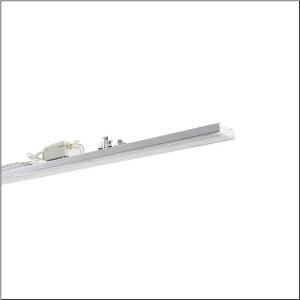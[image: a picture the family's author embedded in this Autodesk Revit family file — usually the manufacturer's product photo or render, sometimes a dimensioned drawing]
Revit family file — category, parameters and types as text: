
# Revit family: licross_11_recessed_extreme_mo_51te18dv4e5ge
name_source: partatom
category: Lighting Fixtures
units: mm (PartAtom-declared; Revit-internal decimal feet)

## family parameters
Cut with Voids When Loaded = No
Host = Face
Light Source = No
Part Type = Normal
Room Calculation Point = No
Round Connector Dimension = Use Diameter
Shared = No

## types (1)
- --- (1 x LED, 14980 lm, 84.5 W, 4000K)
    Apparent Load = 85 VA
    CIE Flux Codes = 83 96 99 100 100
    Color Rendering = 80
    Color Temperature = 4000K
    Default Elevation = 1800 mm
    Description = Licross 11 Recessed extreme MO, luminaire insert, of sheet steel, galvanised, coil coated, white, length: 2.250mm, width: 66mm, height: 67mm, LED rated luminous flux: 14.980lm, light colour: 840, SDCM (Standard Deviation of Colour Matching)MacAdam ≤ 2 SDCM (initial), control gear: DALI 2, with plug, 5-pole, with phase selection, mains connection: 220..240V, AC, 50/60Hz, rated input power: 85W, internal wiring halogen-free, primary light control with lens, of plastic, primary optical cover: cover, of PMMA, light emission: direct distribution, primary light characteristic: symmetric, protection rating (complete): IP54, insulation class (complete): insulation class I (protective earthing), certification: CE, ENEC, VDE, UKCA, protection symbol: D if used in an environment with non-conductive dust loads with corresponding accessories, impact resistance: IK06, permissible ambient temperature for indoor applications: -25..+45°C, corresponds to IFS (International Featured Standards) requirements for safety and quality in the food industry, reducing of maximum allowable ambient temperature of 5°C with ceiling mounting, LABS conformity tested according to VDMA 24364:2018-05, The light source and the operating device comply with the requirements of the Ecodesign Regulation (EU) 2019/2020 and are replaceable in accordance with this regulation, packaging unit: 1 piece
    Height = 58 mm
    Lamp = 1 x LED
    Lamp Light Flux = 14980 lm
    Lamp Power = 84.5 W
    Lamp count = 1
    Length = 2250 mm
    Luminous efficacy = 177 lm/W
    Manufacturer = Siteco
    ModVariant = No
    Model = 51TE18DV4E5GE
    Mounting Place = Ceiling
    Mounting Type = Pendant
    Number of Poles = 1
    OnlyDefault = Yes
    Power Factor = 1
    Product Name = Licross 11 Recessed extreme MO
    Product group = luminaire insert | ceiling pendant
    ProductGroupID = 901
    Protection Class = Protection class I
    Protection Degree = IP 54
    RLX_Detail_Level = 1
    RLX_Emergency_Light_Flux = 0 lm
    RLX_Emergency_Type = 0
    RLX_Emergency_Type_DB = No
    RlxData = <blob elided: 30013 chars, md5=170b6d26>
    Socket = socket
    Standby Power = 0 W
    System Light Flux = 14980 lm
    System Power = 85 W
    Type Comments = factory setting: luminous flux: 100 % | dim-lin: 254 | 380 mA
    Type Image = l_1296930.jpg
    URL = http://relux.com
    VarID = @adj_095181
    Voltage = 0 V
    Weight = 0.00 kg
    Width = 66 mm

## geometry (parser evidence)
native form markers: Blend x4, Sweep x8
no freeform markers — native parametric forms only
